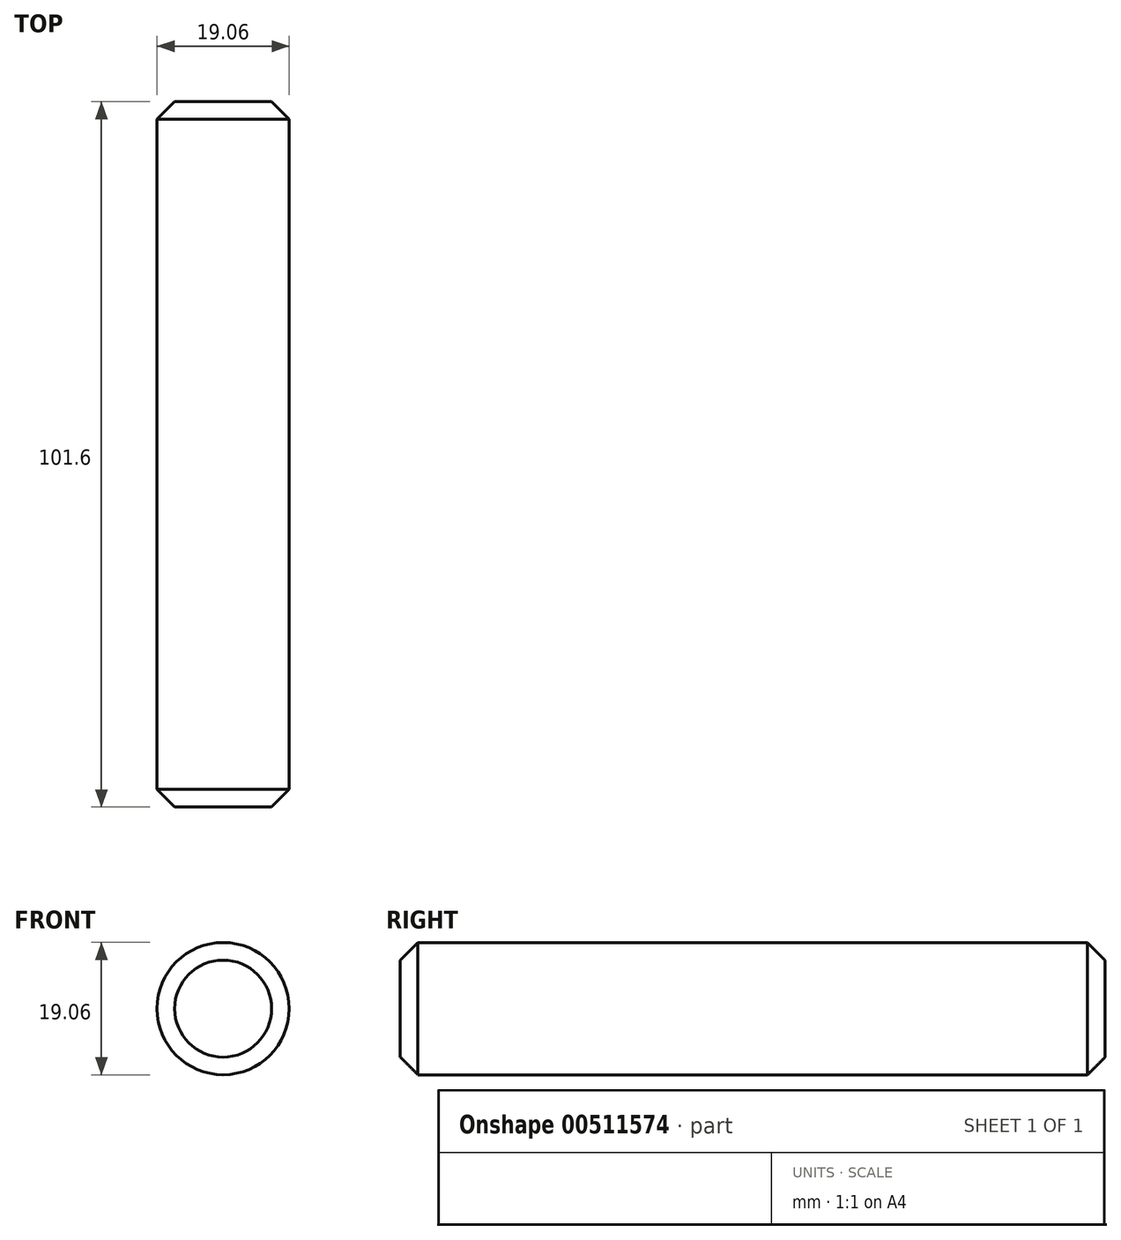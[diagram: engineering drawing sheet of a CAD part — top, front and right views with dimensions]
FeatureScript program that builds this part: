
annotation { "Feature Type Name" : "Feature", "Feature Type Description" : "" }
export const myFeature = defineFeature(function(context is Context, id is Id, definition is map)
    precondition{}
    {
        {
            var Q0;
            Q0=qCreatedBy(makeId("Front.planeOp"),FACE);
            var sketch = newSketch(context, id + "F0", { "sketchPlane" : qUnion([Q0])});
            skCircle(sketch, "E0", {"center": v(0, 0) * mm, "radius": 9.53 * mm});
            skSolve(sketch);
        }
        {
            var Q0;
            Q0 = qSketchRegion(id + "F0", true);
            extrude(context, id + "F1", {"entities" : qUnion([Q0]), "endBound" : BoundingType.SYMMETRIC, "depth" : 101.6 * mm});
        }
        {
            var Q0;
            Q0=makeQuery(id+"F1.opExtrude","CAP_EDGE",EDGE,{"disambiguationData":[OSD([sQuery(id+"F0.wireOp",EDGE,"E0")])],"isStart":true});
            var Q1;
            Q1=makeQuery(id+"F1.opExtrude","CAP_EDGE",EDGE,{"disambiguationData":[OSD([sQuery(id+"F0.wireOp",EDGE,"E0")])],"isStart":false});
            chamfer(context, id + "F2", {"entities" : qUnion([Q0, Q1]), "width" : 2.54 * mm, "tangentPropagation" : true});
        }
    });
